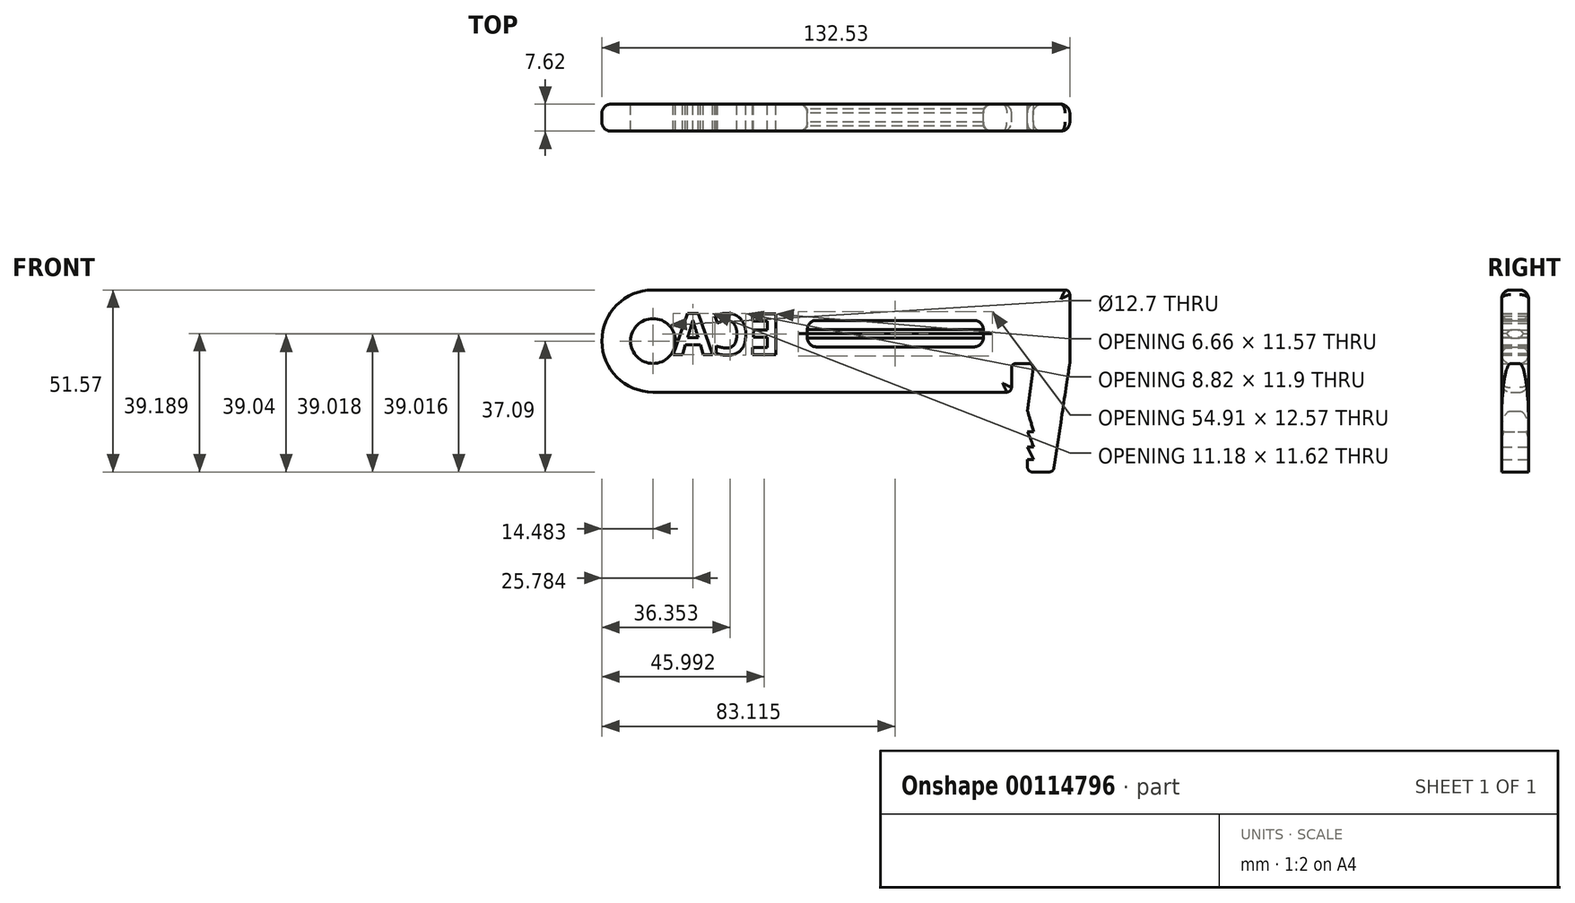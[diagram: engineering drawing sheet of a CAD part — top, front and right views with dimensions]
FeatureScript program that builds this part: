
annotation { "Feature Type Name" : "Feature", "Feature Type Description" : "" }
export const myFeature = defineFeature(function(context is Context, id is Id, definition is map)
    precondition{}
    {
        {
            var Q0;
            Q0=qCreatedBy(makeId("Front.planeOp"),FACE);
            var sketch = newSketch(context, id + "F5", { "sketchPlane" : qUnion([Q0])});
            skLineSegment(sketch, "E0", {"start": v(-61.68, 51.57) * mm, "end": v(55.05, 51.57) * mm});
            skLineSegment(sketch, "E1", {"start": v(56.37, 50.25) * mm, "end": v(56.37, 30.74) * mm});
            skLineSegment(sketch, "E2", {"start": v(56.37, 30.74) * mm, "end": v(51.85, 1.08) * mm});
            skLineSegment(sketch, "E3", {"start": v(50.6, 0) * mm, "end": v(45.68, 0) * mm});
            skLineSegment(sketch, "E4", {"start": v(44.41, 1.27) * mm, "end": v(44.41, 3.51) * mm});
            skLineSegment(sketch, "E5", {"start": v(44.41, 3.51) * mm, "end": v(46.15, 3.51) * mm});
            skLineSegment(sketch, "E6", {"start": v(46.15, 3.51) * mm, "end": v(44.41, 7.08) * mm});
            skLineSegment(sketch, "E7", {"start": v(44.41, 7.08) * mm, "end": v(46.15, 7.08) * mm});
            skLineSegment(sketch, "E8", {"start": v(46.15, 7.08) * mm, "end": v(44.41, 11.43) * mm});
            skLineSegment(sketch, "E9", {"start": v(44.41, 11.43) * mm, "end": v(46.15, 11.43) * mm});
            skLineSegment(sketch, "E10", {"start": v(46.15, 11.43) * mm, "end": v(44.41, 17.28) * mm});
            skLineSegment(sketch, "E11", {"start": v(44.41, 17.28) * mm, "end": v(45.95, 29.25) * mm});
            skLineSegment(sketch, "E12", {"start": v(44.64, 30.74) * mm, "end": v(41.2, 30.74) * mm});
            skLineSegment(sketch, "E13", {"start": v(39.87, 29.42) * mm, "end": v(39.87, 23.93) * mm});
            skLineSegment(sketch, "E14", {"start": v(38.54, 22.6) * mm, "end": v(-61.68, 22.6) * mm});
            skArc(sketch, "E15", {"start": v(-61.68, 51.57) * mm, "mid": v(-76.16, 37.1) * mm, "end": v(-61.68, 22.6) * mm});
            skCircle(sketch, "E16", {"center": v(-61.68, 37.1) * mm, "radius": 6.35 * mm});
            skPoint(sketch, "E17.visualSharp", {"position": v(44.41, 0) * mm});
            skArc(sketch, "E17.filletArc", {"start": v(44.41, 1.27) * mm, "mid": v(44.78, 0.37) * mm, "end": v(45.68, 0) * mm});
            skPoint(sketch, "E18.visualSharp", {"position": v(51.68, 0) * mm});
            skArc(sketch, "E18.filletArc", {"start": v(50.6, 0) * mm, "mid": v(51.42, 0.3) * mm, "end": v(51.85, 1.08) * mm});
            skPoint(sketch, "E19.visualSharp", {"position": v(46.15, 30.74) * mm});
            skArc(sketch, "E19.filletArc", {"start": v(45.95, 29.25) * mm, "mid": v(45.63, 30.3) * mm, "end": v(44.64, 30.74) * mm});
            skPoint(sketch, "E20.visualSharp", {"position": v(39.87, 30.74) * mm});
            skArc(sketch, "E20.filletArc", {"start": v(41.2, 30.74) * mm, "mid": v(40.26, 30.35) * mm, "end": v(39.87, 29.42) * mm});
            skPoint(sketch, "E21.visualSharp", {"position": v(39.87, 22.6) * mm});
            skArc(sketch, "E21.filletArc", {"start": v(38.54, 22.6) * mm, "mid": v(39.48, 23) * mm, "end": v(39.87, 23.93) * mm});
            skPoint(sketch, "E22.visualSharp", {"position": v(56.37, 51.57) * mm});
            skArc(sketch, "E22.filletArc", {"start": v(56.37, 50.25) * mm, "mid": v(55.98, 51.19) * mm, "end": v(55.05, 51.57) * mm});
            skSolve(sketch);
        }
        {
            var Q0;
            Q0=makeQuery(id+"F5.imprint","IMPRINT",FACE,{"disambiguationData":[TD([[makeQuery(id+"F5.imprint","IMPRINT",EDGE,{"derivedFrom":sQuery(id+"F5.wireOp",EDGE,"E0")}),-1.0]])]});
            extrude(context, id + "F0", {"entities" : qUnion([Q0]), "endBound" : BoundingType.SYMMETRIC, "depth" : 7.62 * mm});
        }
        {
            var Q0;
            Q0=makeQuery(id+"F0.opExtrude","SWEPT_FACE",FACE,{"disambiguationData":[OSD([sQuery(id+"F5.wireOp",EDGE,"E0")])]});
            fillet(context, id + "F6", {"entities" : qUnion([Q0]), "radius" : 2.54 * mm, "tangentPropagation" : true, "allowEdgeOverflow" : false});
        }
        {
            var Q0;
            Q0=makeQuery(id+"F0.opExtrude","CAP_FACE",FACE,{"disambiguationData":[OSD([sQuery(id+"F5.wireOp",EDGE,"E0"),sQuery(id+"F5.wireOp",EDGE,"E1"),sQuery(id+"F5.wireOp",EDGE,"E2"),sQuery(id+"F5.wireOp",EDGE,"E3"),sQuery(id+"F5.wireOp",EDGE,"E4"),sQuery(id+"F5.wireOp",EDGE,"E5"),sQuery(id+"F5.wireOp",EDGE,"E6"),sQuery(id+"F5.wireOp",EDGE,"E7"),sQuery(id+"F5.wireOp",EDGE,"E8"),sQuery(id+"F5.wireOp",EDGE,"E9"),sQuery(id+"F5.wireOp",EDGE,"E10"),sQuery(id+"F5.wireOp",EDGE,"E11"),sQuery(id+"F5.wireOp",EDGE,"E12"),sQuery(id+"F5.wireOp",EDGE,"E13"),sQuery(id+"F5.wireOp",EDGE,"E14"),sQuery(id+"F5.wireOp",EDGE,"E15"),sQuery(id+"F5.wireOp",EDGE,"E16"),sQuery(id+"F5.wireOp",EDGE,"E17.filletArc"),sQuery(id+"F5.wireOp",EDGE,"E18.filletArc"),sQuery(id+"F5.wireOp",EDGE,"E19.filletArc"),sQuery(id+"F5.wireOp",EDGE,"E20.filletArc"),sQuery(id+"F5.wireOp",EDGE,"E21.filletArc"),sQuery(id+"F5.wireOp",EDGE,"E22.filletArc")])],"isStart":false});
            var sketch = newSketch(context, id + "F7", { "sketchPlane" : qUnion([Q0])});
            skLineSegment(sketch, "E23.bottom", {"start": v(-17.96, 42.93) * mm, "end": v(31.87, 42.93) * mm});
            skLineSegment(sketch, "E23.top", {"start": v(-17.96, 35.45) * mm, "end": v(31.87, 35.45) * mm});
            skLineSegment(sketch, "E23.left", {"start": v(-17.96, 42.93) * mm, "end": v(-17.96, 35.45) * mm});
            skLineSegment(sketch, "E23.right", {"start": v(31.87, 42.93) * mm, "end": v(31.87, 35.45) * mm});
            skSolve(sketch);
        }
        {
            var Q0;
            Q0 = qSketchRegion(id + "F7", true);
            extrude(context, id + "F1", {"entities" : qUnion([Q0]), "operationType" : NewBodyOperationType.REMOVE, "endBound" : BoundingType.SYMMETRIC, "depth" : 25.4 * mm});
        }
        {
            var Q0;
            Q0=makeQuery(id+"F1.boolean.opBoolean","COPY",FACE,{"derivedFrom":makeQuery(id+"F1.opExtrude","SWEPT_FACE",FACE,{"disambiguationData":[OSD([sQuery(id+"F7.wireOp",EDGE,"E23.top")])]})});
            fillet(context, id + "F2", {"entities" : qUnion([Q0]), "radius" : 2.54 * mm, "tangentPropagation" : true, "allowEdgeOverflow" : false});
        }
        {
            var Q0;
            Q0=makeQuery(id+"F1.boolean.opBoolean","COPY",FACE,{"derivedFrom":makeQuery(id+"F1.opExtrude","SWEPT_FACE",FACE,{"disambiguationData":[OSD([sQuery(id+"F7.wireOp",EDGE,"E23.bottom")])]})});
            fillet(context, id + "F8", {"entities" : qUnion([Q0]), "radius" : 2.54 * mm, "tangentPropagation" : true, "allowEdgeOverflow" : false});
        }
        {
            var Q1;
            Q1=makeQuery(id+"F1.boolean.opBoolean","COPY",FACE,{"derivedFrom":makeQuery(id+"F1.opExtrude","SWEPT_FACE",FACE,{"disambiguationData":[OSD([sQuery(id+"F7.wireOp",EDGE,"E23.right")])]})});
            var Q2;
            Q2=makeQuery(id+"F1.boolean.opBoolean","COPY",FACE,{"derivedFrom":makeQuery(id+"F1.opExtrude","SWEPT_FACE",FACE,{"disambiguationData":[OSD([sQuery(id+"F7.wireOp",EDGE,"E23.left")])]})});
            loft(context, id + "F9", {"sheetProfilesArray" : [{ "sheetProfileEntities" : qUnion([Q1]) }, { "sheetProfileEntities" : qUnion([Q2]) }]});
        }
        {
            var Q0;
            Q0=makeQuery(id+"F0.opExtrude","CAP_FACE",FACE,{"disambiguationData":[OSD([sQuery(id+"F5.wireOp",EDGE,"E0"),sQuery(id+"F5.wireOp",EDGE,"E1"),sQuery(id+"F5.wireOp",EDGE,"E2"),sQuery(id+"F5.wireOp",EDGE,"E3"),sQuery(id+"F5.wireOp",EDGE,"E4"),sQuery(id+"F5.wireOp",EDGE,"E5"),sQuery(id+"F5.wireOp",EDGE,"E6"),sQuery(id+"F5.wireOp",EDGE,"E7"),sQuery(id+"F5.wireOp",EDGE,"E8"),sQuery(id+"F5.wireOp",EDGE,"E9"),sQuery(id+"F5.wireOp",EDGE,"E10"),sQuery(id+"F5.wireOp",EDGE,"E11"),sQuery(id+"F5.wireOp",EDGE,"E12"),sQuery(id+"F5.wireOp",EDGE,"E13"),sQuery(id+"F5.wireOp",EDGE,"E14"),sQuery(id+"F5.wireOp",EDGE,"E15"),sQuery(id+"F5.wireOp",EDGE,"E16"),sQuery(id+"F5.wireOp",EDGE,"E17.filletArc"),sQuery(id+"F5.wireOp",EDGE,"E18.filletArc"),sQuery(id+"F5.wireOp",EDGE,"E19.filletArc"),sQuery(id+"F5.wireOp",EDGE,"E20.filletArc"),sQuery(id+"F5.wireOp",EDGE,"E21.filletArc"),sQuery(id+"F5.wireOp",EDGE,"E22.filletArc")])],"isStart":true});
            var sketch = newSketch(context, id + "F10", { "sketchPlane" : qUnion([Q0])});
            skText(sketch, "E24", { "text": "ECA", "fontName": "OpenSans-Bold.ttf"});
            const initialGuessFQ1xlFFU3axFfiKw3_2  = {"E24": [0.02538, 0.03323, 1, 0, 0.01167]};
            skSetInitialGuess(sketch, initialGuessFQ1xlFFU3axFfiKw3_2);
            skSolve(sketch);
        }
        {
            var Q0;
            Q0=makeQuery(id+"F10.imprint","IMPRINT",FACE,{"disambiguationData":[TD([[makeQuery(id+"F10.imprint","IMPRINT",EDGE,{"derivedFrom":sQuery(id+"F10.wireOp",EDGE,"E24.sketch_text.stroke-27")}),-1.0]])]});
            var Q1;
            Q1=makeQuery(id+"F10.imprint","IMPRINT",FACE,{"disambiguationData":[TD([[makeQuery(id+"F10.imprint","IMPRINT",EDGE,{"derivedFrom":sQuery(id+"F10.wireOp",EDGE,"E24.sketch_text.stroke-0")}),-1.0]])]});
            var Q2;
            Q2=makeQuery(id+"F10.imprint","IMPRINT",FACE,{"disambiguationData":[TD([[makeQuery(id+"F10.imprint","IMPRINT",EDGE,{"derivedFrom":sQuery(id+"F10.wireOp",EDGE,"E24.sketch_text.stroke-12")}),-1.0]])]});
            extrude(context, id + "F3", {"entities" : qUnion([Q0, Q1, Q2]), "operationType" : NewBodyOperationType.REMOVE, "endBound" : BoundingType.SYMMETRIC, "oppositeDirection" : true, "depth" : 25.4 * mm});
        }
        {
            var Q0;
            Q0=sQuery(id+"F5.wireOp",EDGE,"E16");
            extrude(context, id + "F4", {"bodyType" : ToolBodyType.SURFACE, "surfaceEntities" : qUnion([Q0]), "oppositeDirection" : true, "depth" : 25.4 * mm});
        }
    });
